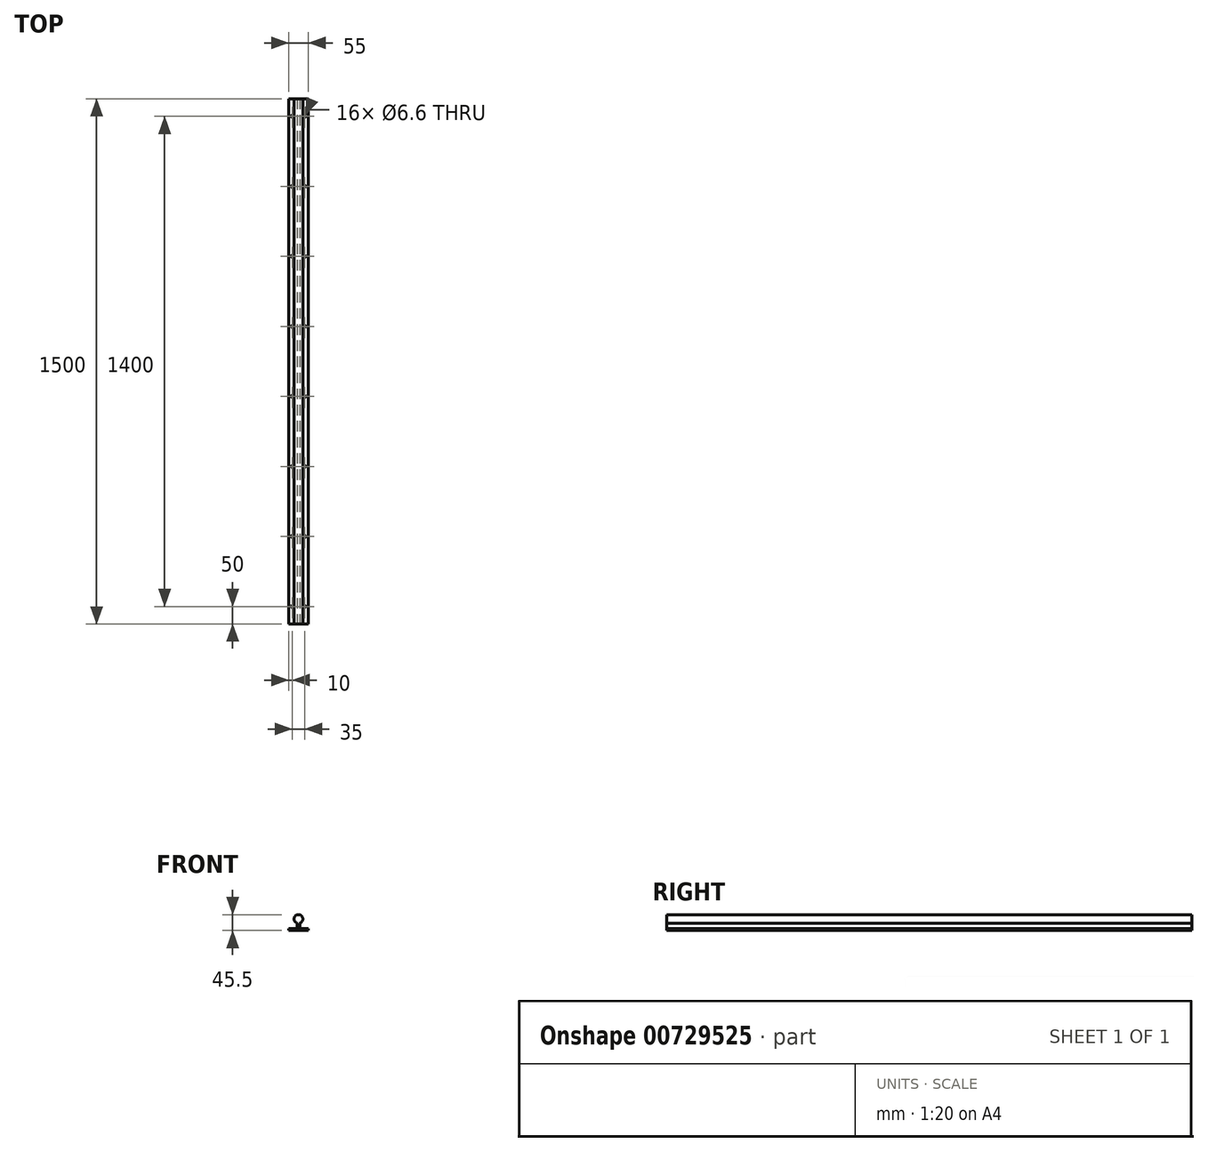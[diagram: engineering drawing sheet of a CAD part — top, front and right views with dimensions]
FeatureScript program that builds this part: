
annotation { "Feature Type Name" : "Feature", "Feature Type Description" : "" }
export const myFeature = defineFeature(function(context is Context, id is Id, definition is map)
    precondition{}
    {
        {
            var Q0;
            Q0=qCreatedBy(makeId("Front.planeOp"),FACE);
            var sketch = newSketch(context, id + "F0", { "sketchPlane" : qUnion([Q0])});
            skLineSegment(sketch, "E0.bottom", {"start": v(27.5, 3) * mm, "end": v(4, 3) * mm});
            skLineSegment(sketch, "E0.top", {"start": v(27.5, -3) * mm, "end": v(-27.5, -3) * mm});
            skLineSegment(sketch, "E0.left", {"start": v(27.5, 3) * mm, "end": v(27.5, -3) * mm});
            skLineSegment(sketch, "E0.right", {"start": v(-27.5, 3) * mm, "end": v(-27.5, -3) * mm});
            skPoint(sketch, "E0.middle", {"position": v(0, 0) * mm});
            skLineSegment(sketch, "E1.left", {"start": v(-4, 3) * mm, "end": v(-4, 18.16) * mm});
            skLineSegment(sketch, "E1.right", {"start": v(4, 3) * mm, "end": v(4, 18.16) * mm});
            skLineSegment(sketch, "E2", {"start": v(0, 50.09) * mm, "end": v(0, -27) * mm, "construction": true});
            skArc(sketch, "E3", {"start": v(4, 18.16) * mm, "mid": v(0, 42.5) * mm, "end": v(-4, 18.16) * mm});
            skLineSegment(sketch, "E4.trimOffspring", {"start": v(-4, 3) * mm, "end": v(-27.5, 3) * mm});
            skSolve(sketch);
        }
        {
            var Q0;
            Q0=qCreatedBy(makeId("Top.planeOp"),FACE);
            var sketch = newSketch(context, id + "F1", { "sketchPlane" : qUnion([Q0])});
            skLineSegment(sketch, "E5", {"start": v(-27.5, 0) * mm, "end": v(-27.5, 1500) * mm});
            skLineSegment(sketch, "E6", {"start": v(-27.5, 1500) * mm, "end": v(27.5, 1500) * mm});
            skLineSegment(sketch, "E7", {"start": v(27.5, 1500) * mm, "end": v(27.5, 0) * mm});
            skLineSegment(sketch, "E8", {"start": v(17.5, 2225.2) * mm, "end": v(17.5, -125.2) * mm, "construction": true});
            skCircle(sketch, "E9", {"center": v(17.5, 50) * mm, "radius": 3.3 * mm});
            skCircle(sketch, "E10", {"center": v(17.5, 250) * mm, "radius": 3.3 * mm});
            skCircle(sketch, "E11", {"center": v(17.5, 1050) * mm, "radius": 3.3 * mm});
            skCircle(sketch, "E12", {"center": v(17.5, 450) * mm, "radius": 3.3 * mm});
            skCircle(sketch, "E13", {"center": v(17.5, 650) * mm, "radius": 3.3 * mm});
            skCircle(sketch, "E14", {"center": v(17.5, 850) * mm, "radius": 3.3 * mm});
            skCircle(sketch, "E15", {"center": v(17.5, 1250) * mm, "radius": 3.3 * mm});
            skCircle(sketch, "E16", {"center": v(17.5, 1450) * mm, "radius": 3.3 * mm});
            skLineSegment(sketch, "E17", {"start": v(0, 1690.05) * mm, "end": v(0, 0) * mm, "construction": true});
            skPoint(sketch, "E18.end.orphan", {"position": v(-115.2, 0) * mm});
            skLineSegment(sketch, "E19.MirrorCS", {"start": v(-17.5, 2225.2) * mm, "end": v(-17.5, -125.2) * mm, "construction": true});
            skCircle(sketch, "E20.MirrorC", {"center": v(-17.5, 50) * mm, "radius": 3.3 * mm});
            skCircle(sketch, "E21.MirrorC", {"center": v(-17.5, 250) * mm, "radius": 3.3 * mm});
            skCircle(sketch, "E22.MirrorC", {"center": v(-17.5, 450) * mm, "radius": 3.3 * mm});
            skCircle(sketch, "E23.MirrorC", {"center": v(-17.5, 650) * mm, "radius": 3.3 * mm});
            skCircle(sketch, "E24.MirrorC", {"center": v(-17.5, 850) * mm, "radius": 3.3 * mm});
            skCircle(sketch, "E25.MirrorC", {"center": v(-17.5, 1450) * mm, "radius": 3.3 * mm});
            skCircle(sketch, "E26.MirrorC", {"center": v(-17.5, 1250) * mm, "radius": 3.3 * mm});
            skCircle(sketch, "E27.MirrorC", {"center": v(-17.5, 1050) * mm, "radius": 3.3 * mm});
            skSolve(sketch);
        }
        {
            var Q0;
            Q0=makeQuery(id+"F0.imprint","IMPRINT",FACE,{"disambiguationData":[TD([[makeQuery(id+"F0.imprint","IMPRINT",EDGE,{"derivedFrom":sQuery(id+"F0.wireOp",EDGE,"E0.bottom")}),1.0]])]});
            extrude(context, id + "F2", {"entities" : qUnion([Q0]), "oppositeDirection" : true, "depth" : 1500 * mm, "offsetDistance" : 25 * mm});
        }
        {
            var Q0;
            Q0 = qSketchRegion(id + "F1", true);
            extrude(context, id + "F3", {"entities" : qUnion([Q0]), "operationType" : NewBodyOperationType.REMOVE, "oppositeDirection" : true, "depth" : 6 * mm, "offsetDistance" : 25 * mm, "symmetric" : true});
        }
    });
